FCSTD DOCUMENT  (FreeCAD 0.16R)
Label: CommCopyRear
License: All rights reserved
LicenseURL: http://en.wikipedia.org/wiki/All_rights_reserved
objects: Sketcher::SketchObject×1
note: 1 computed .brp shape members not serialized (recipe doc carries the construction recipe); baked Part::Feature solids carry a one-line shape summary decoded from their .brp

FEATURE [Sketcher::SketchObject] Sketch
  sketch-geometry (15):
    g0: LineSegment [constr] StartX=-67.5 StartY=0 StartZ=0 EndX=67.5 EndY=0 EndZ=0
    g1: LineSegment [constr] StartX=0 StartY=0 StartZ=0 EndX=0 EndY=375 EndZ=0
    g2: LineSegment [constr] StartX=-34 StartY=375 StartZ=0 EndX=34 EndY=375 EndZ=0
    g3: LineSegment [constr] StartX=18.668 StartY=29 StartZ=0 EndX=18.668 EndY=-29 EndZ=0
    g4: LineSegment [constr] StartX=-34 StartY=392.5 StartZ=0 EndX=34 EndY=392.5 EndZ=0
    g5: LineSegment [constr] StartX=34 StartY=392.5 StartZ=0 EndX=34 EndY=357.5 EndZ=0
    g6: LineSegment [constr] StartX=34 StartY=357.5 StartZ=0 EndX=-34 EndY=357.5 EndZ=0
    g7: LineSegment [constr] StartX=-34 StartY=357.5 StartZ=0 EndX=-34 EndY=392.5 EndZ=0
    g8: Circle [constr] CenterX=0 CenterY=224 CenterZ=0 NormalX=0 NormalY=0 NormalZ=1 Radius=30
    g9: LineSegment [constr] StartX=-34.6976 StartY=254 StartZ=0 EndX=31.2416 EndY=254 EndZ=0
    g10: LineSegment [constr] StartX=29.5 StartY=55 StartZ=0 EndX=29.5 EndY=-55 EndZ=0
    g11: LineSegment [constr] StartX=34 StartY=375 StartZ=0 EndX=99.7449 EndY=375 EndZ=0
    g12: LineSegment [constr] StartX=41 StartY=375 StartZ=0 EndX=41 EndY=425 EndZ=0
    g13: LineSegment [constr] StartX=41 StartY=375 StartZ=0 EndX=41 EndY=325 EndZ=0
    g14: LineSegment [constr] StartX=41 StartY=375 StartZ=0 EndX=25.6498 EndY=-0.083247 EndZ=0
  constraints (44):
    c: PointOnObject(g0,g-1)
    c: Distance(g0) = 135
    c: Symmetric(g0,g0,g-2)
    c: Coincident(g1,g-1)
    c: Vertical(g1)
    c: Distance(g1) = 375
    c: Distance(g2) = 68
    c: Symmetric(g2,g2,g1)
    c: PointOnObject(g1,g2)
    c: Vertical(g3)
    c: Distance(g0,g3) = 48.832
    c: Symmetric(g3,g3,g0)
    c: Distance(g3) = 58
    c: Coincident(g4,g5)
    c: Coincident(g5,g6)
    c: Coincident(g6,g7)
    c: Coincident(g7,g4)
    c: Horizontal(g4)
    c: Horizontal(g6)
    c: Vertical(g5)
    c: Vertical(g7)
    c: PointOnObject(g2,g5)
    c: PointOnObject(g2,g7)
    c: Symmetric(g5,g4,g2)
    c: Distance(g7) = 35
    c: Radius(g8) = 30
    c: PointOnObject(g8,g1)
    c: Horizontal(g9)
    c: Tangent(g9,g8)
    c: DistanceY(g9) = 254
    c: Vertical(g10)
    c: Distance(g0,g10) = 38
    c: Symmetric(g10,g10,g0)
    c: Distance(g10) = 110
    c: Coincident(g11,g2)
    c: Horizontal(g11)
    c: PointOnObject(g12,g11)
    c: Coincident(g13,g12)
    c: Vertical(g13)
    c: Vertical(g12)
    c: Distance(g13) = 50
    c: Equal(g13,g12)
    c: Coincident(g14,g12)
    c: Distance(g1,g12) = 41
